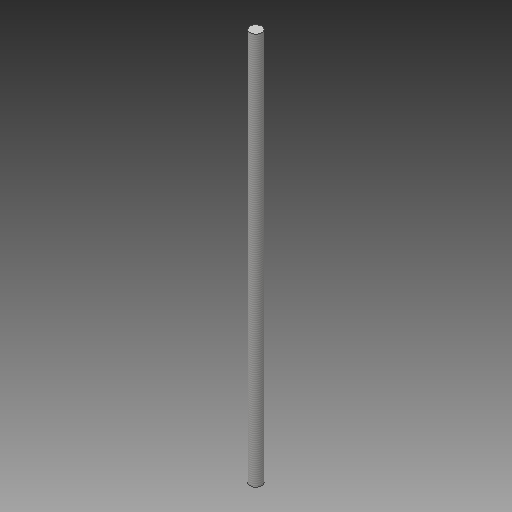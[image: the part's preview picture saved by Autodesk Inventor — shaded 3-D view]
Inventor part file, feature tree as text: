
AUTODESK INVENTOR PART (.ipt)
format: ipt  version: 2018 (Build 220112000, 112)  size: 94,208 bytes
history: native  units: mm
features: extrude x1, thread x1, sketch x1
ambient origin geometry x8: Origin, YZ Plane, XZ Plane, XY Plane, X Axis, Y Axis, Z Axis, Center Point
bodies: Solid1 (feature_tree)
feature tree (3):
  extrude  "Extrusion1"  Depth=100.0mm TaperAngle=0.0deg
  thread  "Thread1"  [1 undecoded]
  sketch  "Sketch1"  dims[d0=3.0mm d1=100.0mm d2=0.0mm d3=10.0mm d4=0.0mm]
note: 1 required parameter value undecoded (feature->parameter linkage not recoverable at this tier; creation-order binding heuristic only, values carry confidence <= 0.55)
